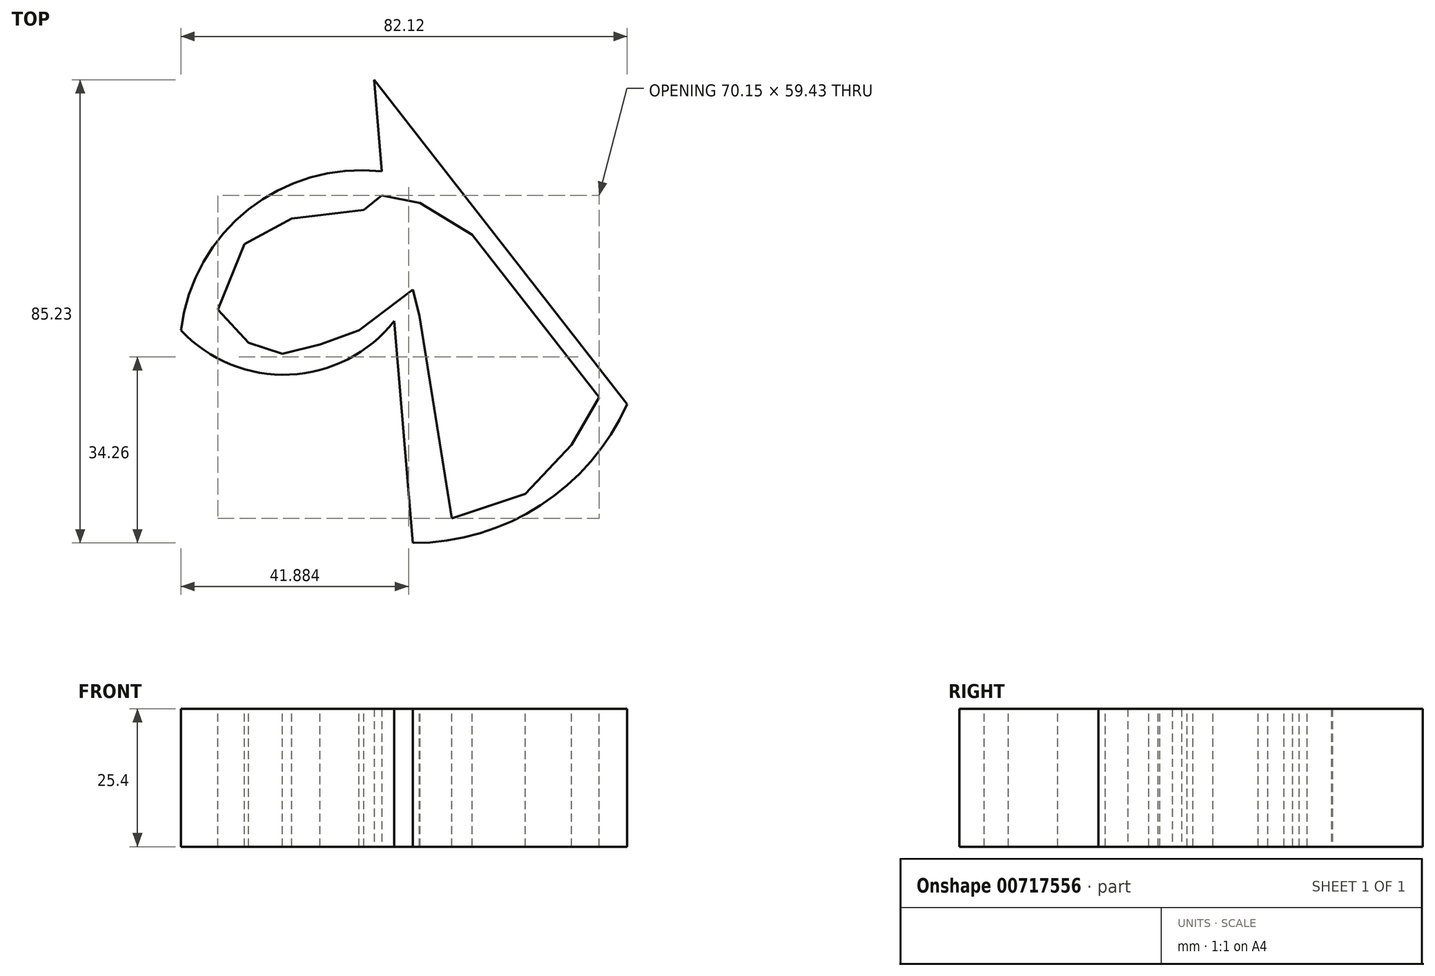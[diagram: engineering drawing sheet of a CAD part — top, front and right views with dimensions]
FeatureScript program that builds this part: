
annotation { "Feature Type Name" : "Feature", "Feature Type Description" : "" }
export const myFeature = defineFeature(function(context is Context, id is Id, definition is map)
    precondition{}
    {
        {
            var Q0;
            Q0=qCreatedBy(makeId("Top.planeOp"),FACE);
            var sketch = newSketch(context, id + "F0", { "sketchPlane" : qUnion([Q0])});
            skArc(sketch, "E0", {"start": v(-42.9, -28.16) * mm, "mid": v(-2.02, -67.17) * mm, "end": v(42.42, -32.27) * mm});
            skLineSegment(sketch, "E1", {"start": v(-38.55, -5.68) * mm, "end": v(39.45, -41.67) * mm});
            skLineSegment(sketch, "E2", {"start": v(39.45, -41.67) * mm, "end": v(-7.13, 18) * mm});
            skLineSegment(sketch, "E3", {"start": v(-7.13, 18) * mm, "end": v(0, -67.22) * mm});
            skSolve(sketch);
        }
        {
            var Q0;
            {var subQ0=sQuery(id+"F0.wireOp",EDGE,"E2");Q0=makeQuery(id+"F0.imprint","IMPRINT",FACE,{"disambiguationData":[TD([[makeQuery(id+"F0.imprint","IMPRINT",EDGE,{"derivedFrom":subQ0}),1.0]])]});}
            var Q1;
            {var subQ1=sQuery(id+"F0.wireOp",EDGE,"E0");var subQ3=sQuery(id+"F0.wireOp",EDGE,"E3");var subQ4=makeQuery(id+"F0.imprint","INTERSECT",VERTEX,{"derivedFrom":[subQ1,subQ3]});Q1=makeQuery(id+"F0.imprint","IMPRINT",FACE,{"disambiguationData":[TD([[makeQuery(id+"F0.imprint","IMPRINT",EDGE,{"disambiguationData":[TD([[subQ4,1.0]])],"derivedFrom":subQ3}),1.0]])]});}
            extrude(context, id + "F1", {"entities" : qUnion([Q0, Q1]), "depth" : 25.4 * mm, "offsetDistance" : 25.4 * mm});
        }
        {
            var Q0;
            Q0=qCreatedBy(makeId("Top.planeOp"),FACE);
            var sketch = newSketch(context, id + "F2", { "sketchPlane" : qUnion([Q0])});
            skArc(sketch, "E4", {"start": v(0, 0) * mm, "mid": v(-27.87, -4.1) * mm, "end": v(-42.67, -28.08) * mm});
            skArc(sketch, "E5", {"start": v(-42.67, -28.08) * mm, "mid": v(-9.53, -31.98) * mm, "end": v(0, 0) * mm});
            skSolve(sketch);
        }
        {
            var Q0;
            Q0 = qSketchRegion(id + "F2", true);
            extrude(context, id + "F3", {"entities" : qUnion([Q0]), "operationType" : NewBodyOperationType.ADD, "depth" : 25.4 * mm, "offsetDistance" : 25.4 * mm});
        }
        {
            var Q0;
            Q0=makeQuery(id+"F3.boolean.opBoolean","MERGE",FACE,{"derivedFrom":[makeQuery(id+"F1.opExtrude","CAP_FACE",FACE,{"disambiguationData":[OSD([sQuery(id+"F0.wireOp",EDGE,"E0"),sQuery(id+"F0.wireOp",EDGE,"E2"),sQuery(id+"F0.wireOp",EDGE,"E3")])],"isStart":false}),makeQuery(id+"F3.opExtrude","CAP_FACE",FACE,{"disambiguationData":[OSD([sQuery(id+"F2.wireOp",EDGE,"E4"),sQuery(id+"F2.wireOp",EDGE,"E5")])],"isStart":false})]});
            var sketch = newSketch(context, id + "F4", { "sketchPlane" : qUnion([Q0])});
            skLineSegment(sketch, "E6", {"start": v(-35.86, -24.26) * mm, "end": v(-30.98, -12.24) * mm});
            skLineSegment(sketch, "E7", {"start": v(-30.98, -12.24) * mm, "end": v(-22.32, -7.5) * mm});
            skLineSegment(sketch, "E8", {"start": v(-22.32, -7.5) * mm, "end": v(-11, -7.5) * mm});
            skLineSegment(sketch, "E9", {"start": v(-11, -7.5) * mm, "end": v(-5.72, -3.24) * mm});
            skLineSegment(sketch, "E10", {"start": v(-5.72, -3.24) * mm, "end": v(1.32, -4.67) * mm});
            skLineSegment(sketch, "E11", {"start": v(1.32, -4.67) * mm, "end": v(10.95, -10.49) * mm});
            skLineSegment(sketch, "E12", {"start": v(10.95, -10.49) * mm, "end": v(34.3, -40.39) * mm});
            skLineSegment(sketch, "E13", {"start": v(34.3, -40.39) * mm, "end": v(29.18, -49.16) * mm});
            skLineSegment(sketch, "E14", {"start": v(29.18, -49.16) * mm, "end": v(20.71, -58.2) * mm});
            skLineSegment(sketch, "E15", {"start": v(20.71, -58.2) * mm, "end": v(7.2, -62.68) * mm});
            skLineSegment(sketch, "E16", {"start": v(7.2, -62.68) * mm, "end": v(1.23, -25.37) * mm});
            skLineSegment(sketch, "E17", {"start": v(1.23, -25.37) * mm, "end": v(0, -20.58) * mm});
            skLineSegment(sketch, "E18", {"start": v(0, -20.58) * mm, "end": v(-9.89, -28.08) * mm});
            skLineSegment(sketch, "E19", {"start": v(-9.89, -28.08) * mm, "end": v(-17.12, -30.69) * mm});
            skLineSegment(sketch, "E20", {"start": v(-17.12, -30.69) * mm, "end": v(-24, -32.4) * mm});
            skLineSegment(sketch, "E21", {"start": v(-24, -32.4) * mm, "end": v(-30.25, -30.39) * mm});
            skLineSegment(sketch, "E22", {"start": v(-30.25, -30.39) * mm, "end": v(-35.86, -24.26) * mm});
            skLineSegment(sketch, "E23", {"start": v(-22.32, -7.5) * mm, "end": v(1.32, -4.67) * mm});
            skSolve(sketch);
        }
        {
            var Q0;
            {var subQ0=sQuery(id+"F4.wireOp",EDGE,"E8");Q0=makeQuery(id+"F4.imprint","IMPRINT",FACE,{"disambiguationData":[TD([[makeQuery(id+"F4.imprint","IMPRINT",EDGE,{"derivedFrom":subQ0}),1.0]])]});}
            var Q1;
            {var subQ0=sQuery(id+"F4.wireOp",EDGE,"E10");Q1=makeQuery(id+"F4.imprint","IMPRINT",FACE,{"disambiguationData":[TD([[makeQuery(id+"F4.imprint","IMPRINT",EDGE,{"derivedFrom":subQ0}),-1.0]])]});}
            var Q2;
            Q2=makeQuery(id+"F4.imprint","IMPRINT",FACE,{"disambiguationData":[TD([[makeQuery(id+"F4.imprint","IMPRINT",EDGE,{"derivedFrom":sQuery(id+"F4.wireOp",EDGE,"E6")}),-1.0]])]});
            extrude(context, id + "F5", {"entities" : qUnion([Q0, Q1, Q2]), "operationType" : NewBodyOperationType.REMOVE, "oppositeDirection" : true, "depth" : 25.4 * mm, "offsetDistance" : 25.4 * mm});
        }
    });
